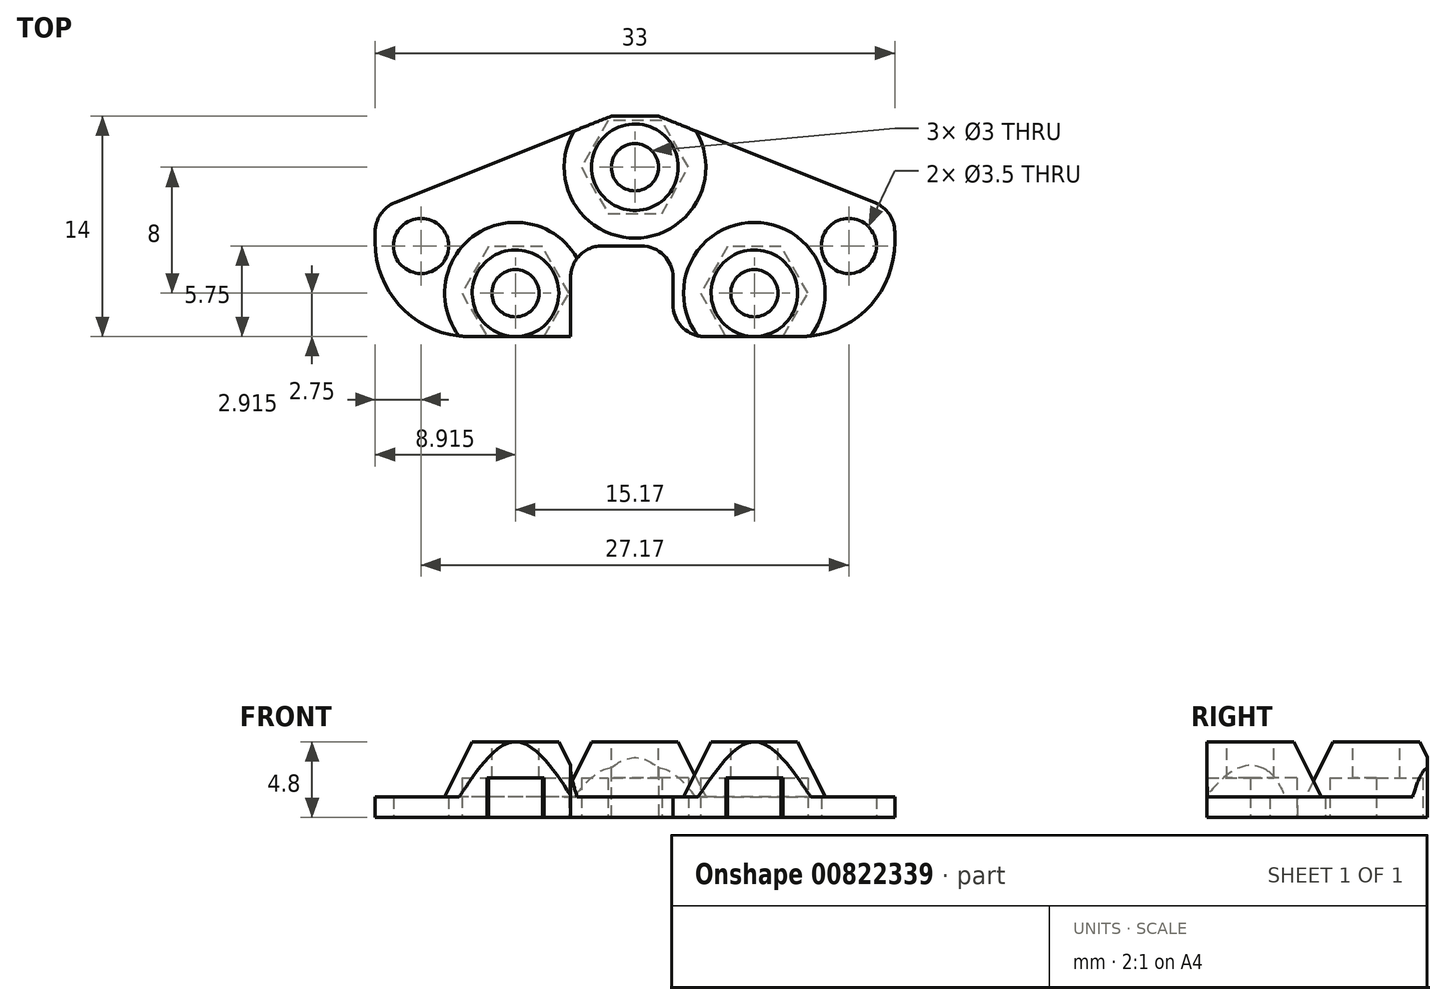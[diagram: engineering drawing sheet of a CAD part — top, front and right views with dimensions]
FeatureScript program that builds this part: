
annotation { "Feature Type Name" : "Feature", "Feature Type Description" : "" }
export const myFeature = defineFeature(function(context is Context, id is Id, definition is map)
    precondition{}
    {
        {
            var Q0;
            Q0=qCreatedBy(makeId("Top.planeOp"),FACE);
            var sketch = newSketch(context, id + "F0", { "sketchPlane" : qUnion([Q0])});
            skLineSegment(sketch, "E0.bottom", {"start": v(-16.5, 8.25) * mm, "end": v(16.5, 8.25) * mm});
            skLineSegment(sketch, "E0.top", {"start": v(-16.5, -5.75) * mm, "end": v(16.5, -5.75) * mm});
            skLineSegment(sketch, "E0.left", {"start": v(-16.5, 8.25) * mm, "end": v(-16.5, -5.75) * mm});
            skLineSegment(sketch, "E0.right", {"start": v(16.5, 8.25) * mm, "end": v(16.5, -5.75) * mm});
            skCircle(sketch, "E1", {"center": v(-13.59, 0) * mm, "radius": 1.75 * mm});
            skCircle(sketch, "E2", {"center": v(13.59, 0) * mm, "radius": 1.75 * mm});
            skSolve(sketch);
        }
        {
            var Q0;
            Q0=makeQuery(id+"F0.imprint","IMPRINT",FACE,{"disambiguationData":[TD([[makeQuery(id+"F0.imprint","IMPRINT",EDGE,{"derivedFrom":sQuery(id+"F0.wireOp",EDGE,"E0.bottom")}),-1.0]])]});
            extrude(context, id + "F1", {"entities" : qUnion([Q0]), "depth" : 4.8 * mm, "offsetDistance" : 25 * mm});
        }
        {
            var Q0;
            Q0=makeQuery(id+"F1.opExtrude","CAP_FACE",FACE,{"disambiguationData":[OSD([sQuery(id+"F0.wireOp",EDGE,"E0.bottom"),sQuery(id+"F0.wireOp",EDGE,"E0.top"),sQuery(id+"F0.wireOp",EDGE,"E0.left"),sQuery(id+"F0.wireOp",EDGE,"E0.right"),sQuery(id+"F0.wireOp",EDGE,"E1"),sQuery(id+"F0.wireOp",EDGE,"E2")])],"isStart":false});
            var sketch = newSketch(context, id + "F2", { "sketchPlane" : qUnion([Q0])});
            skCircle(sketch, "E3.0", {"center": v(-13.59, 0) * mm, "radius": 1.75 * mm, "construction": true});
            skCircle(sketch, "E4.0", {"center": v(13.59, 0) * mm, "radius": 1.75 * mm, "construction": true});
            skCircle(sketch, "E5", {"center": v(0, 5) * mm, "radius": 1.5 * mm});
            skCircle(sketch, "E6", {"center": v(-7.58, -3) * mm, "radius": 1.5 * mm});
            skCircle(sketch, "E7", {"center": v(7.59, -3) * mm, "radius": 1.5 * mm});
            skCircle(sketch, "E8", {"center": v(-7.58, -3) * mm, "radius": 2.5 * mm});
            skCircle(sketch, "E9", {"center": v(0, 5) * mm, "radius": 2.5 * mm});
            skCircle(sketch, "E10", {"center": v(7.59, -3) * mm, "radius": 2.5 * mm});
            skSolve(sketch);
        }
        {
            var Q0;
            Q0=makeQuery(id+"F1.opExtrude","CAP_FACE",FACE,{"disambiguationData":[OSD([sQuery(id+"F0.wireOp",EDGE,"E0.bottom"),sQuery(id+"F0.wireOp",EDGE,"E0.top"),sQuery(id+"F0.wireOp",EDGE,"E0.left"),sQuery(id+"F0.wireOp",EDGE,"E0.right"),sQuery(id+"F0.wireOp",EDGE,"E1"),sQuery(id+"F0.wireOp",EDGE,"E2")])],"isStart":true});
            var sketch = newSketch(context, id + "F3", { "sketchPlane" : qUnion([Q0])});
            skCircle(sketch, "E11.0", {"center": v(-7.58, 3) * mm, "radius": 2.5 * mm, "construction": true});
            skCircle(sketch, "E12.0", {"center": v(-7.58, 3) * mm, "radius": 1.5 * mm, "construction": true});
            skCircle(sketch, "E13.0", {"center": v(0, -5) * mm, "radius": 2.5 * mm, "construction": true});
            skCircle(sketch, "E14.0", {"center": v(0, -5) * mm, "radius": 1.5 * mm, "construction": true});
            skCircle(sketch, "E15.0", {"center": v(7.59, 3) * mm, "radius": 2.5 * mm, "construction": true});
            skCircle(sketch, "E16.0", {"center": v(7.59, 3) * mm, "radius": 1.5 * mm, "construction": true});
            skCircle(sketch, "E17.cCircle", {"center": v(-7.58, 3) * mm, "radius": 2.95 * mm, "construction": true});
            skLineSegment(sketch, "E17.0", {"start": v(-9.29, 5.95) * mm, "end": v(-5.88, 5.95) * mm});
            skLineSegment(sketch, "E17.1", {"start": v(-5.88, 5.95) * mm, "end": v(-4.18, 3) * mm});
            skLineSegment(sketch, "E17.2", {"start": v(-4.18, 3) * mm, "end": v(-5.88, 0.05) * mm});
            skLineSegment(sketch, "E17.3", {"start": v(-5.88, 0.05) * mm, "end": v(-9.29, 0.05) * mm});
            skLineSegment(sketch, "E17.4", {"start": v(-9.29, 0.05) * mm, "end": v(-11, 3) * mm});
            skLineSegment(sketch, "E17.5", {"start": v(-11, 3) * mm, "end": v(-9.29, 5.95) * mm});
            skPoint(sketch, "E17.0.midPoint", {"position": v(-7.58, 5.95) * mm});
            skCircle(sketch, "E18.cCircle", {"center": v(0, -5) * mm, "radius": 2.95 * mm, "construction": true});
            skLineSegment(sketch, "E18.0", {"start": v(1.7, -7.95) * mm, "end": v(-1.7, -7.95) * mm});
            skLineSegment(sketch, "E18.1", {"start": v(-1.7, -7.95) * mm, "end": v(-3.4, -5) * mm});
            skLineSegment(sketch, "E18.2", {"start": v(-3.4, -5) * mm, "end": v(-1.7, -2.05) * mm});
            skLineSegment(sketch, "E18.3", {"start": v(-1.7, -2.05) * mm, "end": v(1.7, -2.05) * mm});
            skLineSegment(sketch, "E18.4", {"start": v(1.7, -2.05) * mm, "end": v(3.4, -5) * mm});
            skLineSegment(sketch, "E18.5", {"start": v(3.4, -5) * mm, "end": v(1.7, -7.95) * mm});
            skPoint(sketch, "E18.0.midPoint", {"position": v(0, -7.95) * mm});
            skCircle(sketch, "E19.cCircle", {"center": v(7.59, 3) * mm, "radius": 2.95 * mm, "construction": true});
            skLineSegment(sketch, "E19.0", {"start": v(5.88, 5.95) * mm, "end": v(9.29, 5.95) * mm});
            skLineSegment(sketch, "E19.1", {"start": v(9.29, 5.95) * mm, "end": v(11, 3) * mm});
            skLineSegment(sketch, "E19.2", {"start": v(11, 3) * mm, "end": v(9.29, 0.05) * mm});
            skLineSegment(sketch, "E19.3", {"start": v(9.29, 0.05) * mm, "end": v(5.88, 0.05) * mm});
            skLineSegment(sketch, "E19.4", {"start": v(5.88, 0.05) * mm, "end": v(4.18, 3) * mm});
            skLineSegment(sketch, "E19.5", {"start": v(4.18, 3) * mm, "end": v(5.88, 5.95) * mm});
            skPoint(sketch, "E19.0.midPoint", {"position": v(7.59, 5.95) * mm});
            skSolve(sketch);
        }
        {
            var Q0;
            Q0=makeQuery(id+"F2.imprint","IMPRINT",FACE,{"disambiguationData":[TD([[makeQuery(id+"F2.imprint","IMPRINT",EDGE,{"derivedFrom":sQuery(id+"F2.wireOp",EDGE,"E6")}),1.0]])]});
            var Q1;
            Q1=makeQuery(id+"F2.imprint","IMPRINT",FACE,{"disambiguationData":[TD([[makeQuery(id+"F2.imprint","IMPRINT",EDGE,{"derivedFrom":sQuery(id+"F2.wireOp",EDGE,"E5")}),1.0]])]});
            var Q2;
            Q2=makeQuery(id+"F2.imprint","IMPRINT",FACE,{"disambiguationData":[TD([[makeQuery(id+"F2.imprint","IMPRINT",EDGE,{"derivedFrom":sQuery(id+"F2.wireOp",EDGE,"E7")}),1.0]])]});
            var Q3;
            Q3=sQuery(id+"F2.wireOp",EDGE,"E5");
            var Q4;
            Q4=sQuery(id+"F2.wireOp",EDGE,"E6");
            var Q5;
            Q5=sQuery(id+"F2.wireOp",EDGE,"E7");
            extrude(context, id + "F4", {"entities" : qUnion([Q0, Q1, Q2]), "operationType" : NewBodyOperationType.REMOVE, "surfaceEntities" : qUnion([Q3, Q4, Q5]), "endBound" : BoundingType.UP_TO_NEXT, "oppositeDirection" : true, "depth" : 25 * mm, "offsetDistance" : 25 * mm});
        }
        {
            var Q0;
            Q0=makeQuery(id+"F2.imprint","IMPRINT",FACE,{"disambiguationData":[TD([[makeQuery(id+"F2.imprint","IMPRINT",EDGE,{"derivedFrom":sQuery(id+"F2.wireOp",EDGE,"E8")}),-1.0]])]});
            extrude(context, id + "F5", {"entities" : qUnion([Q0]), "operationType" : NewBodyOperationType.REMOVE, "oppositeDirection" : true, "depth" : 3.5 * mm, "offsetDistance" : 25 * mm});
        }
        {
            var Q0;
            Q0=makeQuery(id+"F5.boolean.opBoolean","COPY",EDGE,{"derivedFrom":makeQuery(id+"F5.opExtrude","CAP_EDGE",EDGE,{"disambiguationData":[OSD([sQuery(id+"F2.wireOp",EDGE,"E8")])],"isStart":false})});
            var Q1;
            Q1=makeQuery(id+"F5.boolean.opBoolean","COPY",EDGE,{"derivedFrom":makeQuery(id+"F5.opExtrude","CAP_EDGE",EDGE,{"disambiguationData":[OSD([sQuery(id+"F2.wireOp",EDGE,"E9")])],"isStart":false})});
            var Q2;
            Q2=makeQuery(id+"F5.boolean.opBoolean","COPY",EDGE,{"derivedFrom":makeQuery(id+"F5.opExtrude","CAP_EDGE",EDGE,{"disambiguationData":[OSD([sQuery(id+"F2.wireOp",EDGE,"E10")])],"isStart":false})});
            chamfer(context, id + "F6", {"entities" : qUnion([Q0, Q1, Q2]), "chamferType" : ChamferType.TWO_OFFSETS, "width1" : 4 * mm, "oppositeDirection" : false, "width2" : 2 * mm, "tangentPropagation" : true});
        }
        {
            var Q0;
            Q0=makeQuery(id+"F3.imprint","IMPRINT",FACE,{"disambiguationData":[TD([[makeQuery(id+"F3.imprint","IMPRINT",EDGE,{"derivedFrom":sQuery(id+"F3.wireOp",EDGE,"E17.0")}),-1.0]])]});
            var Q1;
            {var subQ1=sQuery(id+"F3.wireOp",EDGE,"E19.2");Q1=makeQuery(id+"F3.imprint","IMPRINT",FACE,{"disambiguationData":[TD([[makeQuery(id+"F3.imprint","IMPRINT",EDGE,{"derivedFrom":subQ1}),-1.0]])]});}
            var Q2;
            Q2=makeQuery(id+"F3.imprint","IMPRINT",FACE,{"disambiguationData":[TD([[makeQuery(id+"F3.imprint","IMPRINT",EDGE,{"derivedFrom":sQuery(id+"F3.wireOp",EDGE,"E18.0")}),-1.0]])]});
            var Q3;
            {var subQ1=sQuery(id+"F3.wireOp",EDGE,"E17.2");Q3=makeQuery(id+"F3.imprint","IMPRINT",FACE,{"disambiguationData":[TD([[makeQuery(id+"F3.imprint","IMPRINT",EDGE,{"derivedFrom":subQ1}),-1.0]])]});}
            extrude(context, id + "F7", {"entities" : qUnion([Q0, Q1, Q2, Q3]), "operationType" : NewBodyOperationType.REMOVE, "oppositeDirection" : true, "depth" : 2.5 * mm, "offsetDistance" : 25 * mm});
        }
        {
            var Q0;
            Q0=makeQuery(id+"F5.boolean.opBoolean","COPY",FACE,{"derivedFrom":makeQuery(id+"F5.opExtrude","CAP_FACE",FACE,{"disambiguationData":[OSD([sQuery(id+"F0.wireOp",EDGE,"E0.bottom"),sQuery(id+"F0.wireOp",EDGE,"E0.top"),sQuery(id+"F0.wireOp",EDGE,"E0.left"),sQuery(id+"F0.wireOp",EDGE,"E0.right"),sQuery(id+"F0.wireOp",EDGE,"E1"),sQuery(id+"F0.wireOp",EDGE,"E2"),sQuery(id+"F2.wireOp",EDGE,"E8"),sQuery(id+"F2.wireOp",EDGE,"E9"),sQuery(id+"F2.wireOp",EDGE,"E10")])],"isStart":false})});
            var sketch = newSketch(context, id + "F8", { "sketchPlane" : qUnion([Q0])});
            skLineSegment(sketch, "E20.bottom", {"start": v(-4.08, -5.75) * mm, "end": v(2.41, -5.75) * mm});
            skLineSegment(sketch, "E20.top", {"start": v(-4.09, 0) * mm, "end": v(2.41, 0) * mm});
            skLineSegment(sketch, "E20.left", {"start": v(-4.08, -5.75) * mm, "end": v(-4.09, 0) * mm});
            skLineSegment(sketch, "E20.right", {"start": v(2.41, -5.75) * mm, "end": v(2.41, 0) * mm});
            skCircle(sketch, "E21.0", {"center": v(-13.59, 0) * mm, "radius": 1.75 * mm, "construction": true});
            skSolve(sketch);
        }
        {
            var Q0;
            Q0 = qSketchRegion(id + "F8", true);
            extrude(context, id + "F9", {"entities" : qUnion([Q0]), "operationType" : NewBodyOperationType.REMOVE, "endBound" : BoundingType.SYMMETRIC, "oppositeDirection" : true, "depth" : 25 * mm, "offsetDistance" : 25 * mm});
        }
        {
            var Q0;
            Q0=makeQuery(id+"F1.opExtrude","SWEPT_EDGE",EDGE,{"disambiguationData":[OSD([sQuery(id+"F0.wireOp",EDGE,"E0.top"),sQuery(id+"F0.wireOp",EDGE,"E0.left")])]});
            var Q1;
            Q1=makeQuery(id+"F1.opExtrude","SWEPT_EDGE",EDGE,{"disambiguationData":[OSD([sQuery(id+"F0.wireOp",EDGE,"E0.top"),sQuery(id+"F0.wireOp",EDGE,"E0.right")])]});
            fillet(context, id + "F10", {"entities" : qUnion([Q0, Q1]), "radius" : 6 * mm, "tangentPropagation" : true, "allowEdgeOverflow" : false});
        }
        {
            var Q0;
            Q0=makeQuery(id+"F1.opExtrude","SWEPT_EDGE",EDGE,{"disambiguationData":[OSD([sQuery(id+"F0.wireOp",EDGE,"E0.bottom"),sQuery(id+"F0.wireOp",EDGE,"E0.left")])]});
            var Q1;
            Q1=makeQuery(id+"F1.opExtrude","SWEPT_EDGE",EDGE,{"disambiguationData":[OSD([sQuery(id+"F0.wireOp",EDGE,"E0.bottom"),sQuery(id+"F0.wireOp",EDGE,"E0.right")])]});
            chamfer(context, id + "F11", {"entities" : qUnion([Q0, Q1]), "chamferType" : ChamferType.TWO_OFFSETS, "width1" : 6 * mm, "oppositeDirection" : false, "width2" : 15 * mm, "tangentPropagation" : true});
        }
        {
            var Q0;
            Q0=makeQuery(id+"F9.boolean.opBoolean","COPY",EDGE,{"derivedFrom":makeQuery(id+"F9.opExtrude","SWEPT_EDGE",EDGE,{"disambiguationData":[OSD([sQuery(id+"F8.wireOp",EDGE,"E20.top"),sQuery(id+"F8.wireOp",EDGE,"E20.left")])]})});
            var Q1;
            Q1=makeQuery(id+"F9.boolean.opBoolean","COPY",EDGE,{"derivedFrom":makeQuery(id+"F9.opExtrude","SWEPT_EDGE",EDGE,{"disambiguationData":[OSD([sQuery(id+"F8.wireOp",EDGE,"E20.top"),sQuery(id+"F8.wireOp",EDGE,"E20.right")])]})});
            var Q2;
            Q2=makeQuery(id+"F9.boolean.opBoolean","COPY",EDGE,{"derivedFrom":makeQuery(id+"F9.opExtrude","SWEPT_EDGE",EDGE,{"disambiguationData":[OSD([sQuery(id+"F0.wireOp",EDGE,"E0.top"),sQuery(id+"F8.wireOp",EDGE,"E20.bottom"),sQuery(id+"F8.wireOp",EDGE,"E20.right")])]})});
            var Q3;
            {var subQ0=sQuery(id+"F0.wireOp",EDGE,"E0.right");Q3=makeQuery(id+"F11.opChamfer","BLEND_EDGE",EDGE,{"blendedFrom":[makeQuery(id+"F1.opExtrude","SWEPT_EDGE",EDGE,{"disambiguationData":[OSD([sQuery(id+"F0.wireOp",EDGE,"E0.bottom"),subQ0])]}),makeQuery(id+"F1.opExtrude","SWEPT_FACE",FACE,{"disambiguationData":[OSD([subQ0])]})],"blendedInto":[makeQuery(id+"F1.opExtrude","SWEPT_FACE",FACE,{"disambiguationData":[OSD([subQ0])]})]});}
            var Q4;
            {var subQ0=sQuery(id+"F0.wireOp",EDGE,"E0.left");Q4=makeQuery(id+"F11.opChamfer","BLEND_EDGE",EDGE,{"blendedFrom":[makeQuery(id+"F1.opExtrude","SWEPT_EDGE",EDGE,{"disambiguationData":[OSD([sQuery(id+"F0.wireOp",EDGE,"E0.bottom"),subQ0])]}),makeQuery(id+"F1.opExtrude","SWEPT_FACE",FACE,{"disambiguationData":[OSD([subQ0])]})],"blendedInto":[makeQuery(id+"F1.opExtrude","SWEPT_FACE",FACE,{"disambiguationData":[OSD([subQ0])]})]});}
            fillet(context, id + "F12", {"entities" : qUnion([Q0, Q1, Q2, Q3, Q4]), "radius" : 2 * mm, "tangentPropagation" : true, "allowEdgeOverflow" : false});
        }
    });
